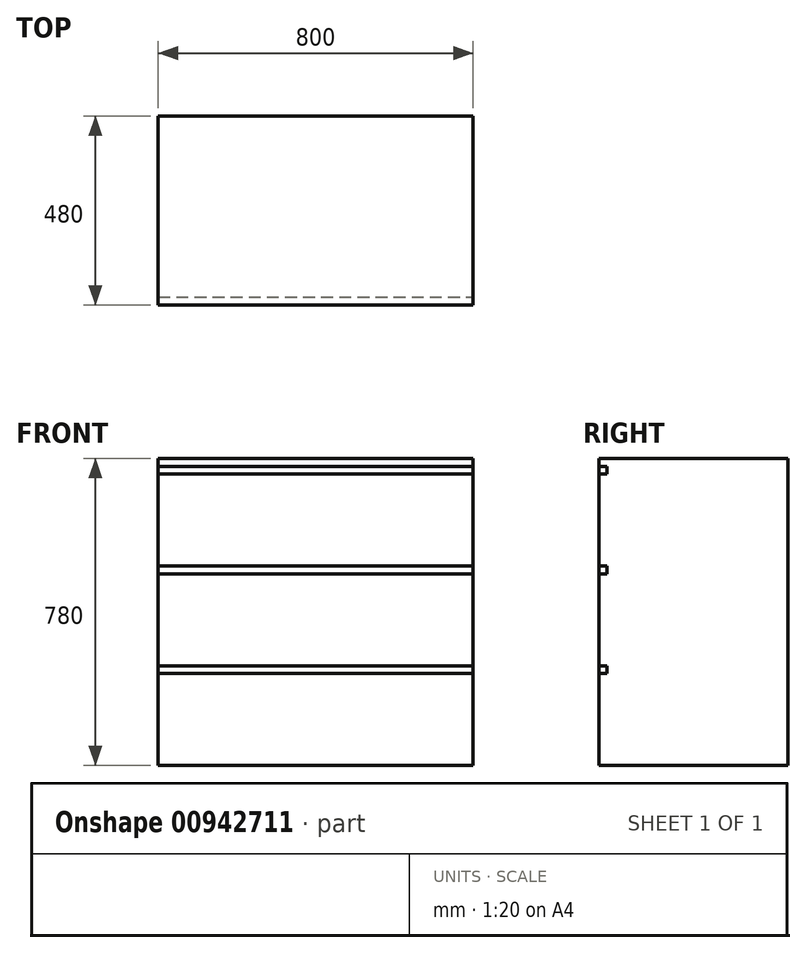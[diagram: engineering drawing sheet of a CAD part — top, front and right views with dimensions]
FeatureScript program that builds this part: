
annotation { "Feature Type Name" : "Feature", "Feature Type Description" : "" }
export const myFeature = defineFeature(function(context is Context, id is Id, definition is map)
    precondition{}
    {
        {
            var Q0;
            Q0=qCreatedBy(makeId("Top.planeOp"),FACE);
            var sketch = newSketch(context, id + "F0", { "sketchPlane" : qUnion([Q0])});
            skLineSegment(sketch, "E0.bottom", {"start": v(-400, -240) * mm, "end": v(400, -240) * mm});
            skLineSegment(sketch, "E0.top", {"start": v(-400, 240) * mm, "end": v(400, 240) * mm});
            skLineSegment(sketch, "E0.left", {"start": v(-400, 240) * mm, "end": v(-400, -240) * mm});
            skLineSegment(sketch, "E0.right", {"start": v(400, 240) * mm, "end": v(400, -240) * mm});
            skLineSegment(sketch, "E1", {"start": v(-400, 0) * mm, "end": v(0, 0) * mm, "construction": true});
            skLineSegment(sketch, "E2", {"start": v(0, 0) * mm, "end": v(400, 0) * mm, "construction": true});
            skLineSegment(sketch, "E3", {"start": v(0, 0) * mm, "end": v(0, 240) * mm, "construction": true});
            skLineSegment(sketch, "E4", {"start": v(0, -240) * mm, "end": v(0, 0) * mm, "construction": true});
            skSolve(sketch);
        }
        {
            var Q0;
            Q0 = qSketchRegion(id + "F0", true);
            extrude(context, id + "F1", {"entities" : qUnion([Q0]), "depth" : 780 * mm, "offsetDistance" : 25 * mm, "symmetric" : true});
        }
        {
            var Q0;
            Q0=makeQuery(id+"F1.opExtrude","SWEPT_FACE",FACE,{"disambiguationData":[OSD([sQuery(id+"F0.wireOp",EDGE,"E0.right")])]});
            var sketch = newSketch(context, id + "F2", { "sketchPlane" : qUnion([Q0])});
            skLineSegment(sketch, "E5", {"start": v(-240, 390) * mm, "end": v(240, 390) * mm});
            skLineSegment(sketch, "E6", {"start": v(240, 390) * mm, "end": v(240, -390) * mm});
            skLineSegment(sketch, "E7", {"start": v(240, -390) * mm, "end": v(-240, -390) * mm});
            skLineSegment(sketch, "E8", {"start": v(-240, -390) * mm, "end": v(-240, -156.67) * mm});
            skLineSegment(sketch, "E9", {"start": v(-240, -156.67) * mm, "end": v(-220, -156.67) * mm});
            skLineSegment(sketch, "E10", {"start": v(-220, -156.67) * mm, "end": v(-220, -136.67) * mm});
            skLineSegment(sketch, "E11", {"start": v(-220, -136.67) * mm, "end": v(-240, -136.67) * mm});
            skLineSegment(sketch, "E12", {"start": v(-240, -136.67) * mm, "end": v(-240, 96.67) * mm});
            skLineSegment(sketch, "E13", {"start": v(-240, 96.67) * mm, "end": v(-220, 96.67) * mm});
            skLineSegment(sketch, "E14", {"start": v(-220, 96.67) * mm, "end": v(-220, 116.67) * mm});
            skLineSegment(sketch, "E15", {"start": v(-220, 116.67) * mm, "end": v(-240, 116.67) * mm});
            skLineSegment(sketch, "E16", {"start": v(-240, 116.67) * mm, "end": v(-240, 350) * mm});
            skLineSegment(sketch, "E17", {"start": v(-240, 350) * mm, "end": v(-220, 350) * mm});
            skLineSegment(sketch, "E18", {"start": v(-220, 350) * mm, "end": v(-220, 370) * mm});
            skLineSegment(sketch, "E19", {"start": v(-220, 370) * mm, "end": v(-240, 370) * mm});
            skLineSegment(sketch, "E20", {"start": v(-240, 370) * mm, "end": v(-240, 390) * mm});
            skSolve(sketch);
        }
        {
            var Q0;
            Q0=makeQuery(id+"F2.imprint","IMPRINT",FACE,{"disambiguationData":[TD([[makeQuery(id+"F2.imprint","IMPRINT",EDGE,{"derivedFrom":sQuery(id+"F2.wireOp",EDGE,"E5")}),1.0]])]});
            extrude(context, id + "F3", {"entities" : qUnion([Q0]), "oppositeDirection" : true, "depth" : 800 * mm, "offsetDistance" : 25 * mm});
        }
    });
